# Revit family: Building-Materials_Glass-Glazing_Vitro-Architectural-Glass_Graylite-II-Monolithic-Glass
name_source: partatom
category: Curtain Panels
units: mm (PartAtom-declared; Revit-internal decimal feet)

## family parameters
Always vertical = Yes
Classification Number = 23.25.20.14.11.11.17
Cut with Voids When Loaded = No
Shared = No

## types (1)
- Graylite II Monolithic
    Analytic Construction = Large single-glazed windows
    Assembly Code = B2020220
    Define Thermal Properties by = Schematic Type
    Description = With its bold, almost‑black look, Graylite® II glass is the solution for applications requiring reduced solar heat gain and a specific aesthetic objective. Graylite® II glass combines superior heat-load reduction and solar control with a distinctive color contrast. Its shading coefficient is among the lowest of any uncoated glass. Its low visible light transmittance (VLT) makes it ideal for glare control and privacy glazing.
    Finish = Glass
    Glass Material = Vitro Architectural-Glass - Graylite II
    Heat Transfer Coefficient (U) = 0.29 BTU/(h·ft²·°F)
    ISO Damage Weighted Transmittance = 0.075
    Keynote = 08900
    Light to Solar Gain = 0.25
    Manufacturer = Vitro Architectural Glass
    Model = Graylite II Monolithic
    Product Guid = 6d1ebaec-7f7e-4029-b841-db9f083e3272
    Product Page URL = https://www.vitroglazings.com
    Product data url = https://www.bimobject.com
    Reflectance (Visible Exterior) = 4
    Reflectance (Visible Interior) = 5
    Shadow Coefficient = 0.42
    Solar Heat Gain Coefficient = 0.36
    Solar Light Transmittance = 0.08
    Thermal Resistance (R) = 8.3333 (h·ft²·°F)/BTU
    Thickness = 0' - 0 1/4"
    U-Value Air (Summer Day) = 0.92 BTU/(h·ft²·°F)
    U-Value Air (Winter Night) = 1.02 BTU/(h·ft²·°F)
    U-Value Argon (Summer Day) = 0 BTU/(h·ft²·°F)
    U-Value Argon (Winter Night) = 0 BTU/(h·ft²·°F)
    URL = https://www.vitroglazings.com
    UV Light Transmittance = 0.02
    Visual Light Transmittance = 0.09

## geometry (parser evidence)
native form markers: Sweep x2
no freeform markers — native parametric forms only
